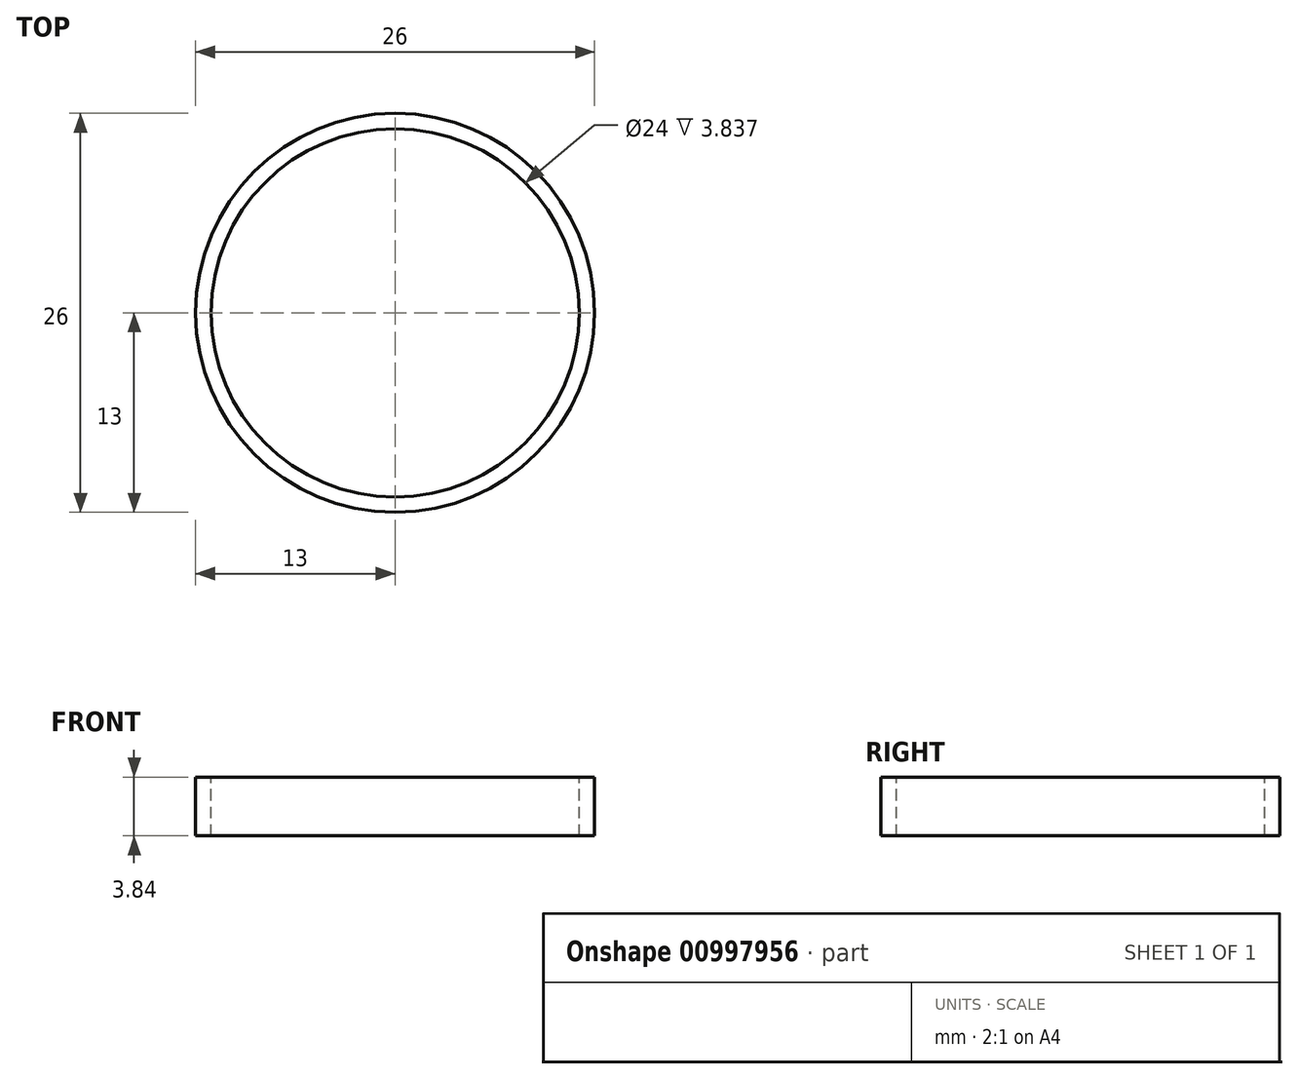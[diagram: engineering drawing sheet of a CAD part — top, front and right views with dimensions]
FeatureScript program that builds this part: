
annotation { "Feature Type Name" : "Feature", "Feature Type Description" : "" }
export const myFeature = defineFeature(function(context is Context, id is Id, definition is map)
    precondition{}
    {
        {
            var Q0;
            Q0=qCreatedBy(makeId("Front.planeOp"),FACE);
            var sketch = newSketch(context, id + "F0", { "sketchPlane" : qUnion([Q0])});
            skLineSegment(sketch, "E0", {"start": v(13, 0) * mm, "end": v(13, 3.84) * mm});
            skLineSegment(sketch, "E1", {"start": v(13, 3.84) * mm, "end": v(12, 3.84) * mm});
            skLineSegment(sketch, "E2", {"start": v(12, 3.84) * mm, "end": v(12, 0) * mm});
            skLineSegment(sketch, "E3", {"start": v(12, 0) * mm, "end": v(13, 0) * mm});
            skLineSegment(sketch, "E4", {"start": v(0, 6.4) * mm, "end": v(0, -1) * mm, "construction": true});
            skSolve(sketch);
        }
        {
            var Q0;
            Q0=makeQuery(id+"F0.imprint","IMPRINT",FACE,{"disambiguationData":[TD([[makeQuery(id+"F0.imprint","IMPRINT",EDGE,{"derivedFrom":sQuery(id+"F0.wireOp",EDGE,"E0")}),1.0]])]});
            var Q1;
            Q1=sQuery(id+"F0.wireOp",EDGE,"E4");
            revolve(context, id + "F1", {"surfaceOperationType" : NewSurfaceOperationType.NEW, "entities" : qUnion([Q0]), "axis" : qUnion([Q1]), "revolveType" : RevolveType.FULL});
        }
    });
